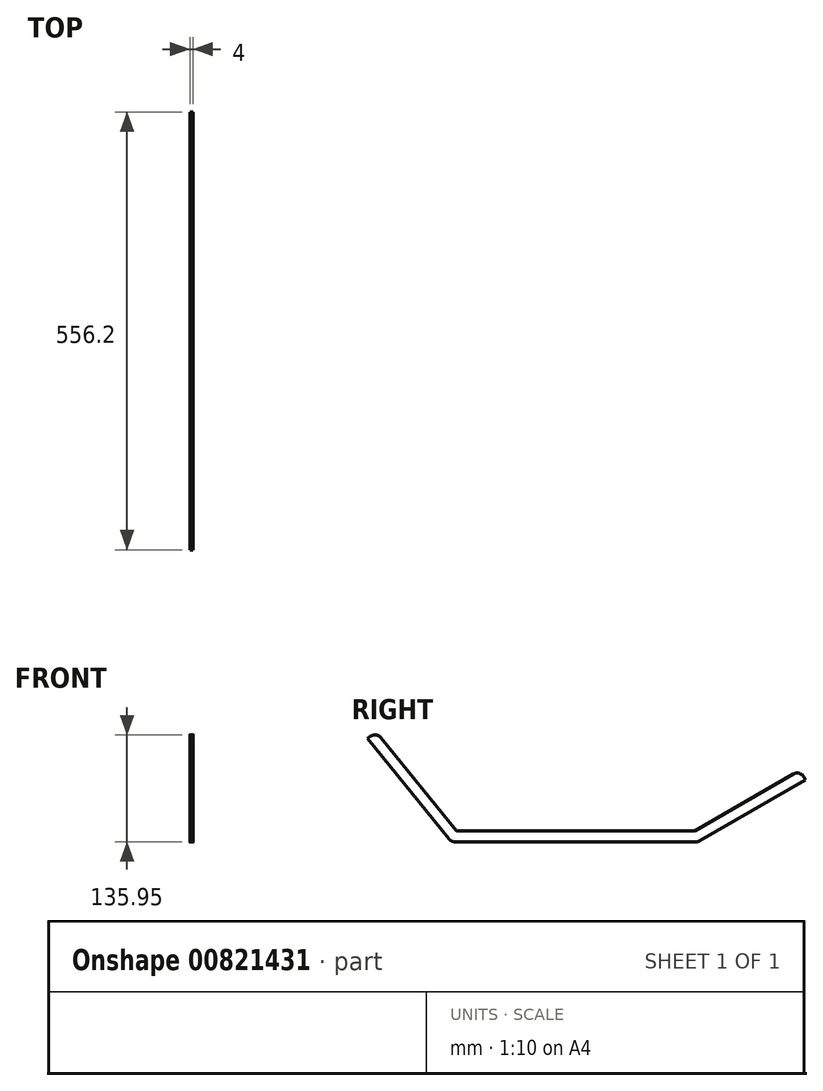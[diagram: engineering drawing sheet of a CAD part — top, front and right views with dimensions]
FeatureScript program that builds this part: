
annotation { "Feature Type Name" : "Feature", "Feature Type Description" : "" }
export const myFeature = defineFeature(function(context is Context, id is Id, definition is map)
    precondition{}
    {
        {
            var Q0;
            Q0=qCreatedBy(makeId("Right.planeOp"),FACE);
            var sketch = newSketch(context, id + "F0", { "sketchPlane" : qUnion([Q0])});
            skLineSegment(sketch, "E0.0", {"start": v(-183.06, -21.6) * mm, "end": v(119.64, -21.6) * mm});
            skLineSegment(sketch, "E1", {"start": v(260.22, 43.4) * mm, "end": v(258.22, 46.87) * mm});
            skLineSegment(sketch, "E2", {"start": v(-295.98, 95.6) * mm, "end": v(-292.87, 98.13) * mm});
            skLineSegment(sketch, "E3", {"start": v(120.71, -35.6) * mm, "end": v(-185.07, -35.6) * mm});
            skLineSegment(sketch, "E4", {"start": v(-184.97, -35.6) * mm, "end": v(-185.07, -35.6) * mm});
            skPoint(sketch, "E5.visualSharp", {"position": v(123.4, -35.6) * mm});
            skArc(sketch, "E5.filletArc", {"start": v(120.71, -35.6) * mm, "mid": v(123.3, -35.25) * mm, "end": v(125.71, -34.25) * mm});
            skPoint(sketch, "E6.visualSharp", {"position": v(-189.74, -35.6) * mm});
            skArc(sketch, "E6.filletArc", {"start": v(-192.74, -31.89) * mm, "mid": v(-189.27, -34.62) * mm, "end": v(-184.97, -35.6) * mm});
            skLineSegment(sketch, "E7", {"start": v(-295.98, 95.6) * mm, "end": v(-192.74, -31.89) * mm});
            skLineSegment(sketch, "E8", {"start": v(-183.06, -21.6) * mm, "end": v(-278.8, 96.65) * mm});
            skLineSegment(sketch, "E9", {"start": v(119.64, -21.6) * mm, "end": v(244.56, 50.53) * mm});
            skLineSegment(sketch, "E10", {"start": v(125.71, -34.25) * mm, "end": v(260.22, 43.4) * mm});
            skPoint(sketch, "E11.visualSharp", {"position": v(253.22, 55.53) * mm});
            skArc(sketch, "E11.filletArc", {"start": v(258.22, 46.87) * mm, "mid": v(252.15, 51.53) * mm, "end": v(244.56, 50.53) * mm});
            skPoint(sketch, "E12.visualSharp", {"position": v(-285.1, 104.42) * mm});
            skArc(sketch, "E12.filletArc", {"start": v(-278.8, 96.65) * mm, "mid": v(-285.53, 100.3) * mm, "end": v(-292.87, 98.13) * mm});
            skSolve(sketch);
        }
        {
            var Q0;
            Q0=makeQuery(id+"F0.imprint","IMPRINT",FACE,{"disambiguationData":[TD([[makeQuery(id+"F0.imprint","IMPRINT",EDGE,{"derivedFrom":sQuery(id+"F0.wireOp",EDGE,"E0.0")}),-1.0]])]});
            extrude(context, id + "F1", {"entities" : qUnion([Q0]), "depth" : 4 * mm, "offsetDistance" : 25 * mm});
        }
    });
